# Revit family: Faucet-Two_Handle-American_Standard-Heritage-7298.152.002
name_source: partatom
category: Plumbing Fixtures
units: mm (PartAtom-declared; Revit-internal decimal feet)

## family parameters
Cut with Voids When Loaded = No
Host = Face
OmniClass Number = 23.45.55.17
OmniClass Title = Mixing Faucets
Part Type = Normal
Room Calculation Point = No
Round Connector Dimension = Use Diameter
Shared = Yes

## types (1)
- 7298.152.002
    ADA Compliant = Yes
    ASME A112.18.1/CSA B125.1 = Yes
    Assembly Code = D2020300
    CW Connection = Yes
    CWFU = 1.5
    Ceramic Disc Valve Cartridges = Yes
    Cold Water Connection Diameter = 1/2"
    Default Elevation = 0"
    Description = Heritage Two Handle Wall Mount Sink Faucet with Brass Spout
    Finish = Brass-American_Standard-002-Polished Chrome
    Flow Rate = 1.5gpm/5.7L/min
    HW Connection = Yes
    HWFU = 1.5
    Hot Water Connection Diameter = 1/2"
    Installation Type = Wall Mounted
    Length = 13 5/8"
    Low Lead = Yes
    Manufacturer = American Standard
    Material = Brass-American_Standard-002-Polished Chrome
    Model = 7298.152
    Price = Prices may vary. Please consult Manufacturer Representative for most up-to-date price list.
    Product Documentation Link = https://americanstandard.box.com
    Product Page URL = https://www.americanstandard-us.com
    Revised Date = 09/09/2021
    Solid Brass Construction = Yes
    URL = https://www.americanstandard-us.com
    Vent Connection = No
    WFU = 2
    Warranty Information URL = https://www.americanstandard-us.com
    Waste Connection = No
    Width = 10 5/8"

## geometry (parser evidence)
native form markers: Sweep x3
no freeform markers — native parametric forms only
